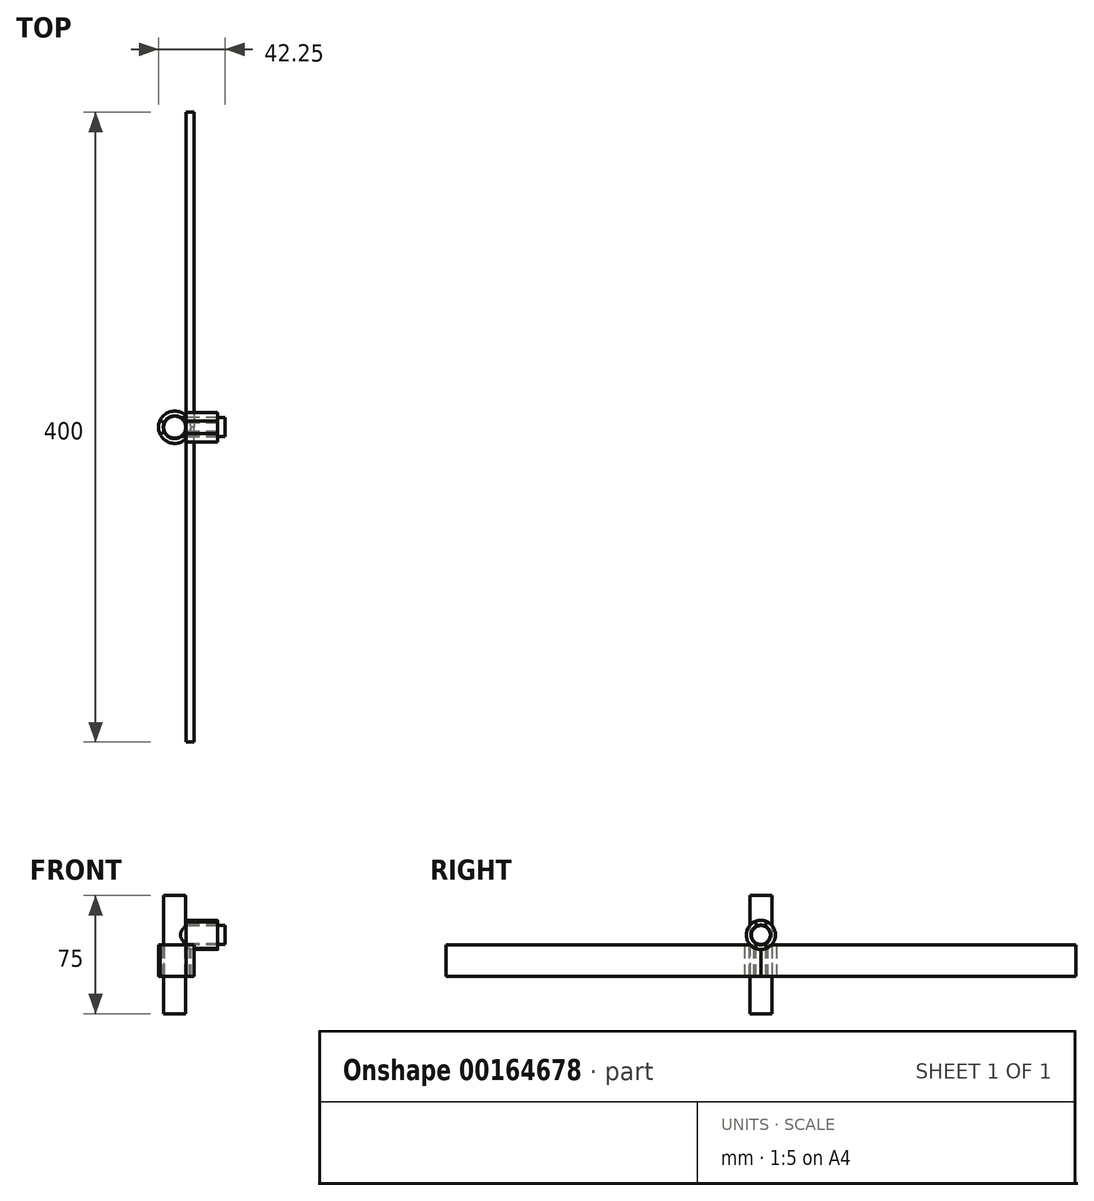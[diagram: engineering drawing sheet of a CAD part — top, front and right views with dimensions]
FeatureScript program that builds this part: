
annotation { "Feature Type Name" : "Feature", "Feature Type Description" : "" }
export const myFeature = defineFeature(function(context is Context, id is Id, definition is map)
    precondition{}
    {
        {
            assignVariable(context, id + "F0", {"name" : "D", "anyValue" : 14});
        }
        {
            assignVariable(context, id + "F1", {"name" : "D2", "anyValue" : 12});
        }
        {
            var Q0;
            Q0=qCreatedBy(makeId("Top.planeOp"),FACE);
            var sketch = newSketch(context, id + "F2", { "sketchPlane" : qUnion([Q0])});
            skCircle(sketch, "E0", {"center": v(0, 0) * mm, "radius": 7 * mm});
            skLineSegment(sketch, "E1", {"start": v(0, 0) * mm, "end": v(0, -41.82) * mm, "construction": true});
            skLineSegment(sketch, "E2", {"start": v(0, 0) * mm, "end": v(204.8, 0) * mm, "construction": true});
            skSolve(sketch);
        }
        {
            var Q0;
            Q0=qCreatedBy(makeId("Right.planeOp"),FACE);
            var sketch = newSketch(context, id + "F3", { "sketchPlane" : qUnion([Q0])});
            skCircle(sketch, "E3", {"center": v(0, 0) * mm, "radius": 6 * mm});
            skSolve(sketch);
        }
        {
            assignVariable(context, id + "F4", {"name" : "L", "anyValue" : 25});
        }
        {
            var Q0;
            Q0=makeQuery(id+"F3.imprint","IMPRINT",FACE,{"disambiguationData":[TD([[makeQuery(id+"F3.imprint","IMPRINT",EDGE,{"derivedFrom":sQuery(id+"F3.wireOp",EDGE,"E3")}),1.0]])]});
            extrude(context, id + "F5", {"entities" : qUnion([Q0]), "depth" : (getVariable(context, 'D') / 2 + getVariable(context, 'L')) * mm});
        }
        {
            var Q0;
            Q0=makeQuery(id+"F2.imprint","IMPRINT",FACE,{"disambiguationData":[TD([[makeQuery(id+"F2.imprint","IMPRINT",EDGE,{"derivedFrom":sQuery(id+"F2.wireOp",EDGE,"E0")}),1.0]])]});
            extrude(context, id + "F6", {"entities" : qUnion([Q0]), "operationType" : NewBodyOperationType.ADD, "depth" : getVariable(context, 'L') * mm});
        }
        {
            var Q0;
            Q0=makeQuery(id+"F2.imprint","IMPRINT",FACE,{"disambiguationData":[TD([[makeQuery(id+"F2.imprint","IMPRINT",EDGE,{"derivedFrom":sQuery(id+"F2.wireOp",EDGE,"E0")}),1.0]])]});
            extrude(context, id + "F7", {"entities" : qUnion([Q0]), "operationType" : NewBodyOperationType.ADD, "oppositeDirection" : true, "depth" : 50 * mm});
        }
        {
            assignVariable(context, id + "F8", {"name" : "W", "anyValue" : 20});
        }
        {
            assignVariable(context, id + "F9", {"name" : "Slack", "anyValue" : 0.25});
        }
        {
            var Q0;
            Q0=qCreatedBy(makeId("Right.planeOp"),FACE);
            cPlane(context, id + "F10", {"entities" : qUnion([Q0]), "cplaneType" : CPlaneType.OFFSET, "offset" : (getVariable(context, 'D') / 2 + getVariable(context, 'Slack')) * mm, "width" : 150 * mm, "height" : 150 * mm});
        }
        {
            var Q0;
            Q0=qCreatedBy(id+"F10.planeOp",FACE);
            var sketch = newSketch(context, id + "F11", { "sketchPlane" : qUnion([Q0])});
            skArc(sketch, "E4", {"start": v(2.64, 5.66) * mm, "mid": v(-6.25, 0) * mm, "end": v(2.64, -5.66) * mm});
            skLineSegment(sketch, "E5", {"start": v(0, 0) * mm, "end": v(2.64, 5.66) * mm, "construction": true});
            skLineSegment(sketch, "E6", {"start": v(2.64, -5.66) * mm, "end": v(0, 0) * mm, "construction": true});
            skLineSegment(sketch, "E7", {"start": v(2.64, -5.66) * mm, "end": v(3.9, -8.38) * mm});
            skLineSegment(sketch, "E8", {"start": v(2.64, 5.66) * mm, "end": v(3.9, 8.38) * mm});
            skArc(sketch, "E9", {"start": v(3.9, 8.38) * mm, "mid": v(-9.25, 0) * mm, "end": v(3.9, -8.38) * mm});
            skSolve(sketch);
        }
        {
            var Q0;
            Q0=makeQuery(id+"F11.imprint","IMPRINT",FACE,{"disambiguationData":[TD([[makeQuery(id+"F11.imprint","IMPRINT",EDGE,{"derivedFrom":sQuery(id+"F11.wireOp",EDGE,"E4")}),-1.0]])]});
            extrude(context, id + "F12", {"entities" : qUnion([Q0]), "depth" : getVariable(context, 'W') * mm});
        }
        {
            var Q0;
            Q0=qCreatedBy(makeId("Top.planeOp"),FACE);
            cPlane(context, id + "F13", {"entities" : qUnion([Q0]), "cplaneType" : CPlaneType.OFFSET, "offset" : (getVariable(context, 'D2') / 2 + getVariable(context, 'Slack')) * mm, "oppositeDirection" : true, "width" : 150 * mm, "height" : 150 * mm});
        }
        {
            var Q0;
            Q0=qCreatedBy(id+"F13.planeOp",FACE);
            var sketch = newSketch(context, id + "F14", { "sketchPlane" : qUnion([Q0])});
            skArc(sketch, "E10", {"start": v(-6.57, 3.06) * mm, "mid": v(0, -7.25) * mm, "end": v(6.57, 3.06) * mm});
            skLineSegment(sketch, "E11", {"start": v(-6.57, 3.06) * mm, "end": v(0, 0) * mm, "construction": true});
            skLineSegment(sketch, "E12", {"start": v(0, 0) * mm, "end": v(6.57, 3.06) * mm, "construction": true});
            skLineSegment(sketch, "E13", {"start": v(-6.57, 3.06) * mm, "end": v(-9.29, 4.33) * mm});
            skLineSegment(sketch, "E14", {"start": v(6.57, 3.06) * mm, "end": v(9.29, 4.33) * mm});
            skArc(sketch, "E15", {"start": v(-9.29, 4.33) * mm, "mid": v(0, -10.25) * mm, "end": v(9.29, 4.33) * mm});
            skSolve(sketch);
        }
        {
            var Q0;
            Q0=makeQuery(id+"F14.imprint","IMPRINT",FACE,{"disambiguationData":[TD([[makeQuery(id+"F14.imprint","IMPRINT",EDGE,{"derivedFrom":sQuery(id+"F14.wireOp",EDGE,"E10")}),-1.0]])]});
            extrude(context, id + "F15", {"entities" : qUnion([Q0]), "oppositeDirection" : true, "depth" : getVariable(context, 'W') * mm});
        }
        {
            var Q0;
            Q0=makeQuery(id+"F12.opExtrude","SWEPT_BODY",BODY,{"disambiguationData":[OSD([sQuery(id+"F11.wireOp",EDGE,"E4"),sQuery(id+"F11.wireOp",EDGE,"E7"),sQuery(id+"F11.wireOp",EDGE,"E8"),sQuery(id+"F11.wireOp",EDGE,"E9")])]});
            var Q1;
            Q1=sQuery(id+"F2.wireOp",EDGE,"E2");
            transform(context, id + "F16", {"entities" : qUnion([Q0]), "transformType" : TransformType.ROTATION, "transformAxis" : qUnion([Q1]), "angle" : 180 * degree, "makeCopy" : false});
        }
        {
            var Q0;
            Q0=qCreatedBy(makeId("Front.planeOp"),FACE);
            var sketch = newSketch(context, id + "F17", { "sketchPlane" : qUnion([Q0])});
            skLineSegment(sketch, "E16.bottom", {"start": v(7.25, -6.25) * mm, "end": v(12.25, -6.25) * mm});
            skLineSegment(sketch, "E16.top", {"start": v(7.25, -26.25) * mm, "end": v(12.25, -26.25) * mm});
            skLineSegment(sketch, "E16.left", {"start": v(7.25, -6.25) * mm, "end": v(7.25, -26.25) * mm});
            skLineSegment(sketch, "E16.right", {"start": v(12.25, -6.25) * mm, "end": v(12.25, -26.25) * mm});
            skSolve(sketch);
        }
        {
            var Q0;
            Q0=makeQuery(id+"F17.imprint","IMPRINT",FACE,{"disambiguationData":[TD([[makeQuery(id+"F17.imprint","IMPRINT",EDGE,{"derivedFrom":sQuery(id+"F17.wireOp",EDGE,"E16.bottom")}),-1.0]])]});
            extrude(context, id + "F18", {"entities" : qUnion([Q0]), "operationType" : NewBodyOperationType.ADD, "depth" : 200 * mm});
        }
        {
            var Q0;
            Q0=makeQuery(id+"F12.opExtrude","SWEPT_BODY",BODY,{"disambiguationData":[OSD([sQuery(id+"F11.wireOp",EDGE,"E4"),sQuery(id+"F11.wireOp",EDGE,"E7"),sQuery(id+"F11.wireOp",EDGE,"E8"),sQuery(id+"F11.wireOp",EDGE,"E9")])]});
            var Q1;
            Q1=qCreatedBy(makeId("Front.planeOp"),FACE);
            mirror(context, id + "F19", {"entities" : qUnion([Q0]), "mirrorPlane" : qUnion([Q1])});
        }
    });
